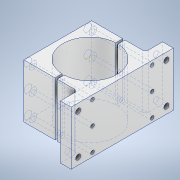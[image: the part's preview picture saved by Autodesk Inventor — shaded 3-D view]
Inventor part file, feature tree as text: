
AUTODESK INVENTOR PART (.ipt)
format: ipt  version: 2020.1 (Build 241239000, 239)  size: 191,488 bytes
history: native  units: mm
features: sketch x5, extrude x3, projected_geometry x3, other x1, fillet x1, hole x1
ambient origin geometry x8: Origin, YZ Plane, XZ Plane, XY Plane, X Axis, Y Axis, Z Axis, Center Point
bodies: Body1 (feature_tree)
feature tree (14):
  other  "Твердое тело1"
  extrude  "Выдавливание1"  Depth=100.0mm
  sketch  "Эскиз2"
  fillet  "Сопряжение1"  Radius=32.0mm
  extrude  "Выдавливание2"  Depth=32.0mm
  hole  "Отверстие1"  [1 undecoded]
  extrude  "Выдавливание3"  Depth=20.0mm
  sketch  "Эскиз1"
  sketch  "Эскиз3"
  projected_geometry  "Спроецированная петля1"
  projected_geometry  "Спроецированная петля2"
  sketch  "Эскиз4"
  projected_geometry  "Спроецированная петля3"
  sketch  "Эскиз5"
note: 1 required parameter value undecoded (feature->parameter linkage not recoverable at this tier; creation-order binding heuristic only, values carry confidence <= 0.55)
